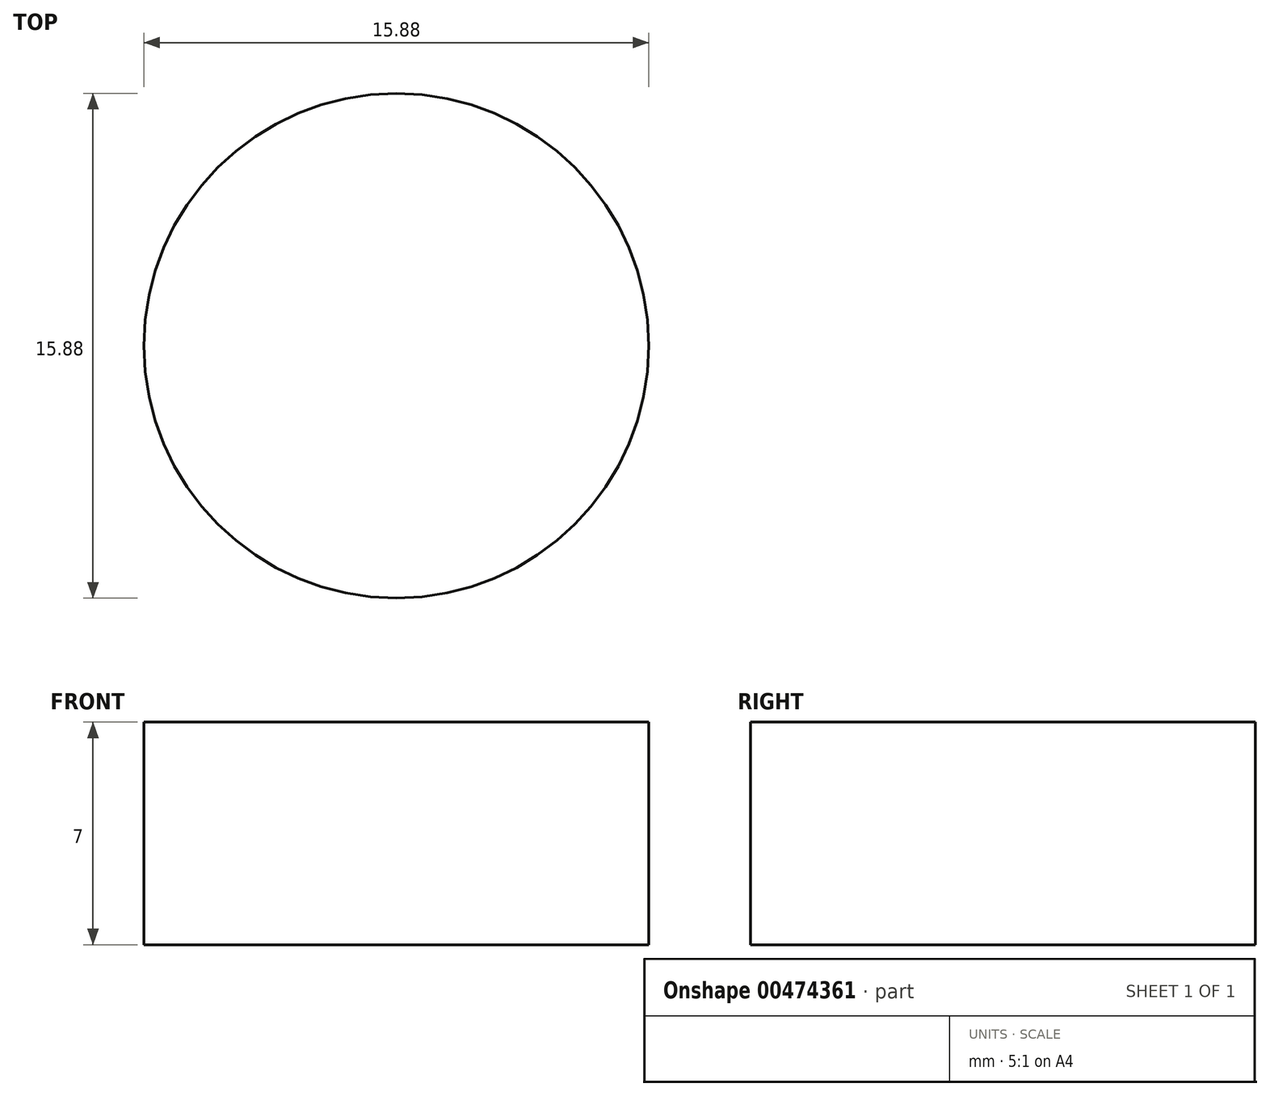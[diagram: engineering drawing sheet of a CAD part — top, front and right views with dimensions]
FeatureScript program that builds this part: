
annotation { "Feature Type Name" : "Feature", "Feature Type Description" : "" }
export const myFeature = defineFeature(function(context is Context, id is Id, definition is map)
    precondition{}
    {
        {
            var Q0;
            Q0=qCreatedBy(makeId("Top.planeOp"),FACE);
            var sketch = newSketch(context, id + "F0", { "sketchPlane" : qUnion([Q0])});
            skCircle(sketch, "E0", {"center": v(0, 0) * mm, "radius": 7.94 * mm});
            skSolve(sketch);
        }
        {
            var Q0;
            Q0 = qSketchRegion(id + "F0", true);
            extrude(context, id + "F1", {"entities" : qUnion([Q0]), "depth" : 7 * mm});
        }
    });
